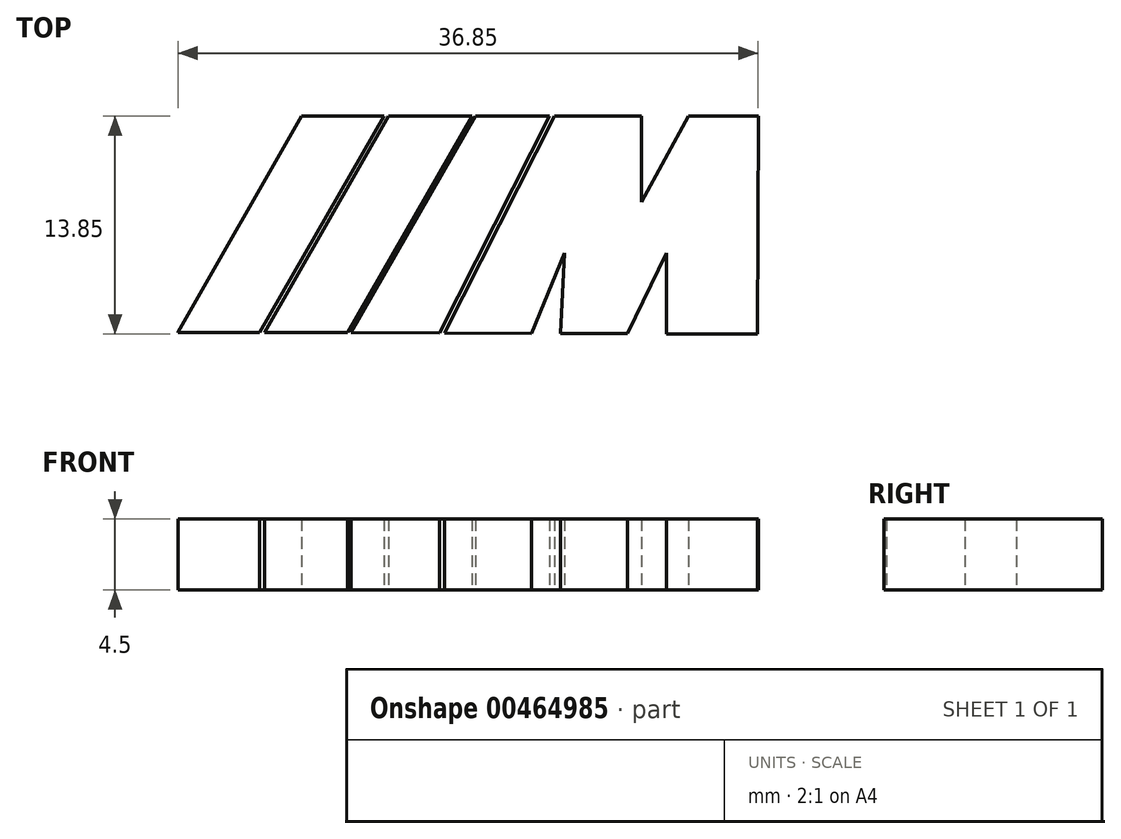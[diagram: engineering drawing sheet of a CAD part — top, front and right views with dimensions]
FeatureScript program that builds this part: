
annotation { "Feature Type Name" : "Feature", "Feature Type Description" : "" }
export const myFeature = defineFeature(function(context is Context, id is Id, definition is map)
    precondition{}
    {
        {
            var Q0;
            Q0=qCreatedBy(makeId("Top.planeOp"),FACE);
            var sketch = newSketch(context, id + "F0", { "sketchPlane" : qUnion([Q0])});
            skLineSegment(sketch, "E0", {"start": v(-40.27, -6.95) * mm, "end": v(-32.43, 6.77) * mm});
            skPoint(sketch, "E1.endSnap0", {"position": v(-37.5, -6.95) * mm});
            skPoint(sketch, "E2.endSnap0", {"position": v(-31.99, -7.14) * mm});
            skPoint(sketch, "E3.endSnap0", {"position": v(-26.48, -7.06) * mm});
            skPoint(sketch, "E4.endSnap0", {"position": v(-20.97, -7.14) * mm});
            skLineSegment(sketch, "E5", {"start": v(-7.85, 6.77) * mm, "end": v(-10.85, 1.3) * mm});
            skLineSegment(sketch, "E6", {"start": v(-15.74, -1.94) * mm, "end": v(-15.98, -7.04) * mm});
            skLineSegment(sketch, "E7", {"start": v(-10.85, 6.77) * mm, "end": v(-10.85, 1.3) * mm});
            skLineSegment(sketch, "E8", {"start": v(-11.54, -6.66) * mm, "end": v(-9.26, -1.94) * mm});
            skLineSegment(sketch, "E9", {"start": v(-7.85, 6.77) * mm, "end": v(-3.43, 6.77) * mm});
            skLineSegment(sketch, "E10", {"start": v(-21.38, 6.77) * mm, "end": v(-16.67, 6.77) * mm});
            skLineSegment(sketch, "E11", {"start": v(-16.37, 6.77) * mm, "end": v(-10.85, 6.77) * mm});
            skLineSegment(sketch, "E12", {"start": v(-32.43, 6.77) * mm, "end": v(-27.2, 6.77) * mm});
            skLineSegment(sketch, "E13", {"start": v(-26.9, 6.77) * mm, "end": v(-21.61, 6.77) * mm});
            skLineSegment(sketch, "E14", {"start": v(-21.38, 6.77) * mm, "end": v(-29.27, -6.99) * mm});
            skLineSegment(sketch, "E15", {"start": v(-29.5, -6.99) * mm, "end": v(-21.61, 6.77) * mm});
            skLineSegment(sketch, "E16", {"start": v(-27.2, 6.77) * mm, "end": v(-35.09, -6.97) * mm});
            skLineSegment(sketch, "E17", {"start": v(-26.9, 6.77) * mm, "end": v(-34.79, -6.97) * mm});
            skLineSegment(sketch, "E18", {"start": v(-16.67, 6.77) * mm, "end": v(-23.67, -7) * mm});
            skLineSegment(sketch, "E19", {"start": v(-23.67, -7) * mm, "end": v(-16.67, 6.77) * mm});
            skLineSegment(sketch, "E20", {"start": v(-23.37, -7.01) * mm, "end": v(-16.37, 6.77) * mm});
            skLineSegment(sketch, "E21", {"start": v(-34.79, -6.97) * mm, "end": v(-29.5, -6.99) * mm});
            skLineSegment(sketch, "E22", {"start": v(-29.27, -6.99) * mm, "end": v(-23.67, -7) * mm});
            skLineSegment(sketch, "E23", {"start": v(-23.37, -7.01) * mm, "end": v(-17.82, -7.03) * mm});
            skLineSegment(sketch, "E24", {"start": v(-17.82, -7.03) * mm, "end": v(-15.74, -1.94) * mm});
            skLineSegment(sketch, "E25", {"start": v(-15.98, -7.04) * mm, "end": v(-11.72, -7.05) * mm});
            skLineSegment(sketch, "E26", {"start": v(-11.54, -6.66) * mm, "end": v(-11.72, -7.05) * mm});
            skLineSegment(sketch, "E27", {"start": v(-9.26, -1.94) * mm, "end": v(-9.26, -7.06) * mm});
            skLineSegment(sketch, "E28", {"start": v(-9.26, -7.06) * mm, "end": v(-3.48, -7.08) * mm});
            skLineSegment(sketch, "E29", {"start": v(-3.48, -7.08) * mm, "end": v(-3.43, 6.77) * mm});
            skLineSegment(sketch, "E30", {"start": v(-40.27, -6.95) * mm, "end": v(-40.28, -6.97) * mm});
            skLineSegment(sketch, "E31", {"start": v(-40.28, -6.97) * mm, "end": v(-35.09, -6.97) * mm});
            skSolve(sketch);
        }
        {
            var Q0;
            Q0=makeQuery(id+"F0.imprint","IMPRINT",FACE,{"disambiguationData":[TD([[makeQuery(id+"F0.imprint","IMPRINT",EDGE,{"derivedFrom":sQuery(id+"F0.wireOp",EDGE,"E5")}),1.0]])]});
            var Q1;
            Q1=makeQuery(id+"F0.imprint","IMPRINT",FACE,{"disambiguationData":[TD([[makeQuery(id+"F0.imprint","IMPRINT",EDGE,{"derivedFrom":sQuery(id+"F0.wireOp",EDGE,"7a2e617c-1076-4560-97de-b42dd3e738cd")}),-1.0]])]});
            var Q2;
            Q2=makeQuery(id+"F0.imprint","IMPRINT",FACE,{"disambiguationData":[TD([[makeQuery(id+"F0.imprint","IMPRINT",EDGE,{"derivedFrom":sQuery(id+"F0.wireOp",EDGE,"8a4a80a8-2528-4ec7-bae5-4b77f74dbabd")}),-1.0]])]});
            var Q3;
            Q3=makeQuery(id+"F0.imprint","IMPRINT",FACE,{"disambiguationData":[TD([[makeQuery(id+"F0.imprint","IMPRINT",EDGE,{"derivedFrom":sQuery(id+"F0.wireOp",EDGE,"E0")}),-1.0]])]});
            var Q4;
            Q4=makeQuery(id+"F0.imprint","IMPRINT",FACE,{"disambiguationData":[TD([[makeQuery(id+"F0.imprint","IMPRINT",EDGE,{"derivedFrom":sQuery(id+"F0.wireOp",EDGE,"E13")}),-1.0]])]});
            var Q5;
            Q5=makeQuery(id+"F0.imprint","IMPRINT",FACE,{"disambiguationData":[TD([[makeQuery(id+"F0.imprint","IMPRINT",EDGE,{"derivedFrom":sQuery(id+"F0.wireOp",EDGE,"E10")}),-1.0]])]});
            extrude(context, id + "F1", {"entities" : qUnion([Q0, Q1, Q2, Q3, Q4, Q5]), "depth" : 4.5 * mm});
        }
    });
